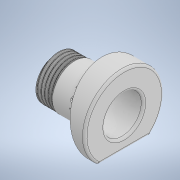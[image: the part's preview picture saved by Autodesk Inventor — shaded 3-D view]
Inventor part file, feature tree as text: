
AUTODESK INVENTOR PART (.ipt)
format: ipt  version: 2021.1 (Build 251245010, 245A)  size: 889,856 bytes
history: native  units: in
note: dims shown in document units (in); Inventor stores cm internally (conversion verified against a paired STEP export)
features: sketch x5, plane x3, fillet x3, extrude x2, revolve x1, helix x1, emboss x1
ambient origin geometry x8: Origin, YZ Plane, XZ Plane, XY Plane, X Axis, Y Axis, Z Axis, Center Point
bodies: Solid1 (feature_tree)
feature tree (16):
  revolve  "Revolution1"  [1 undecoded]
  helix  "Coil1"  [1 undecoded]
  plane  "Work Plane2"
  emboss  "Emboss2"
  plane  "Work Plane4"
  extrude  "Extrusion1"  TaperAngle=90.0deg  [1 undecoded]
  extrude  "Extrusion3"  Depth=0.25in
  fillet  "Fillet1"  [1 undecoded]
  fillet  "Fillet2"  Radius=0.0072in
  fillet  "Fillet3"  [1 undecoded]
  sketch  "Sketch2"  dims[d0=1.1in d1=0.5344in d2=0.125in]
  sketch  "Sketch4"  dims[d3=1.5in d4=90.0deg]
  sketch  "Sketch6"  dims[d5=0.625in d6=0.25in d10=60.0deg d11=0.0072in d12=60.0deg]
  plane  "Work Plane3"
  sketch  "Sketch8"  dims[d13=60.0deg]
  sketch  "Sketch15"  dims[d15=0.1in d16=0.2in d17=0.05in d18=0.6144in d19=0.5494in d20=30.0deg d21=0.1in d22=0.625in d23=0.3937in d24=0.0in d25=90.0deg d26=90.0deg d27=0.0in d28=0.0in d38=0.0906in d39=0.5494in d40=0.6144in d41=0.25in d42=0.05in d43=0.0in d44=0.0825in d45=0.375in d46=1.0in d47=0.0in d57=0.3in d58=0.0in d59=0.0in d60=0.0625in d61=0.0625in d62=0.0625in d53=0.5in d54=0.0344in d55=0.5in d56=0.0344in]
note: 5 required parameter values undecoded (feature->parameter linkage not recoverable at this tier; creation-order binding heuristic only, values carry confidence <= 0.55)